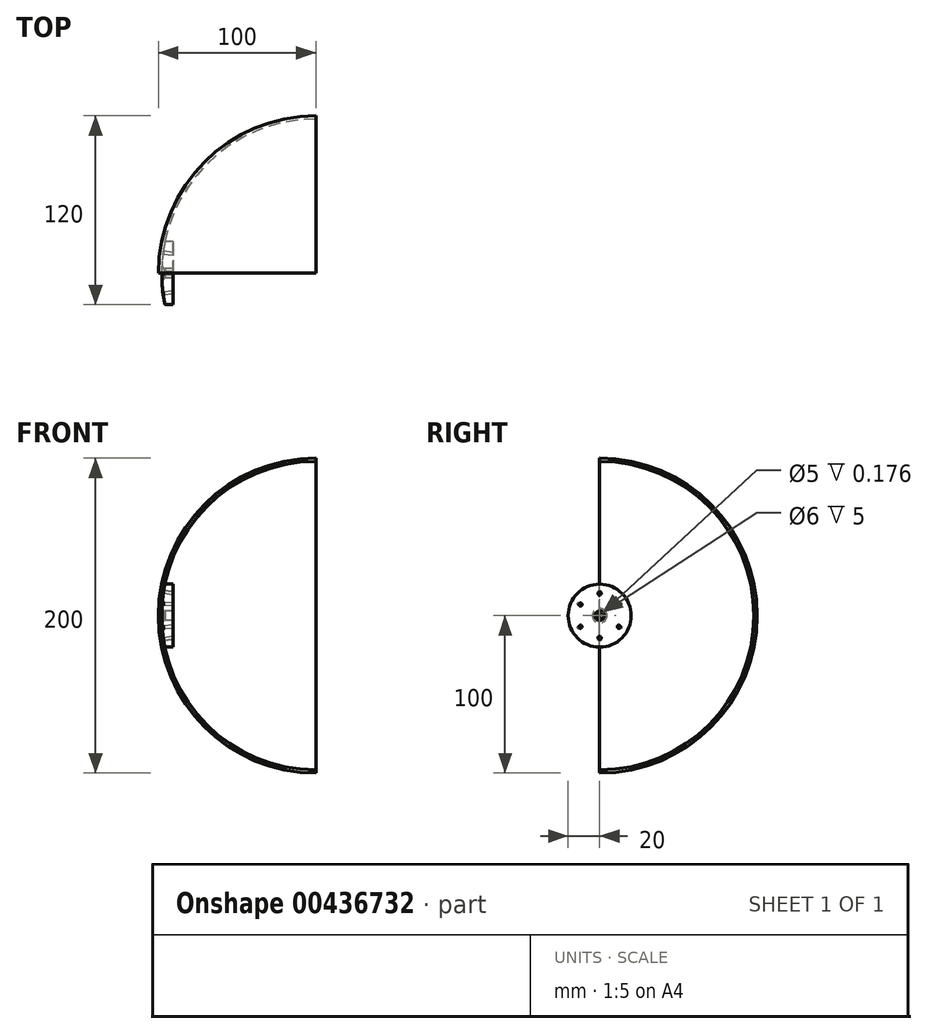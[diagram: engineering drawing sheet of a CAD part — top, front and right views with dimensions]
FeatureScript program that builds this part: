
annotation { "Feature Type Name" : "Feature", "Feature Type Description" : "" }
export const myFeature = defineFeature(function(context is Context, id is Id, definition is map)
    precondition{}
    {
        {
            var Q0;
            Q0=qCreatedBy(makeId("Front.planeOp"),FACE);
            var sketch = newSketch(context, id + "F0", { "sketchPlane" : qUnion([Q0])});
            skLineSegment(sketch, "E0", {"start": v(-108.07, 0) * mm, "end": v(24.36, 0) * mm, "construction": true});
            skLineSegment(sketch, "E1", {"start": v(0, 100) * mm, "end": v(0, 98) * mm});
            skPoint(sketch, "E2.orphan", {"position": v(0, -98) * mm});
            skPoint(sketch, "E3.orphan", {"position": v(0, -100) * mm});
            skArc(sketch, "E4", {"start": v(0, 100) * mm, "mid": v(-70.71, 70.71) * mm, "end": v(-100, 0) * mm});
            skArc(sketch, "E5", {"start": v(0, 98) * mm, "mid": v(-69.3, 69.3) * mm, "end": v(-98, 0) * mm});
            skLineSegment(sketch, "E6", {"start": v(-100, 0) * mm, "end": v(-98, 0) * mm});
            skSolve(sketch);
        }
        {
            var Q0;
            Q0 = qSketchRegion(id + "F0", true);
            var Q1;
            Q1=sQuery(id+"F0.wireOp",EDGE,"E0");
            revolve(context, id + "F1", {"entities" : qUnion([Q0]), "axis" : qUnion([Q1]), "revolveType" : RevolveType.ONE_DIRECTION, "oppositeDirection" : true, "angle" : 180 * degree});
        }
        {
            var Q0;
            Q0=qCreatedBy(makeId("Front.planeOp"),FACE);
            var sketch = newSketch(context, id + "F2", { "sketchPlane" : qUnion([Q0])});
            skArc(sketch, "E7", {"start": v(-95.94, 20) * mm, "mid": v(-97.35, 11.3) * mm, "end": v(-97.97, 2.5) * mm});
            skLineSegment(sketch, "E8", {"start": v(-90.72, 20) * mm, "end": v(-90.72, 3) * mm});
            skLineSegment(sketch, "E9", {"start": v(-95.94, 20) * mm, "end": v(-90.72, 20) * mm});
            skLineSegment(sketch, "E10", {"start": v(-90.72, 3) * mm, "end": v(-95.72, 3) * mm});
            skLineSegment(sketch, "E11", {"start": v(-95.72, 3) * mm, "end": v(-95.72, 2.5) * mm});
            skLineSegment(sketch, "E12", {"start": v(-95.72, 2.5) * mm, "end": v(-97.97, 2.5) * mm});
            skSolve(sketch);
        }
        {
            var Q0;
            Q0 = qSketchRegion(id + "F2", true);
            var Q1;
            Q1=sQuery(id+"F0.wireOp",EDGE,"E0");
            revolve(context, id + "F3", {"entities" : qUnion([Q0]), "axis" : qUnion([Q1]), "revolveType" : RevolveType.FULL});
        }
        {
            var Q0;
            Q0=qCreatedBy(makeId("Front.planeOp"),FACE);
            var sketch = newSketch(context, id + "F4", { "sketchPlane" : qUnion([Q0])});
            skLineSegment(sketch, "E13", {"start": v(-108.32, 16.78) * mm, "end": v(-86.69, 13.43) * mm, "construction": true});
            skPoint(sketch, "E14", {"position": v(-96.85, 15) * mm});
            skLineSegment(sketch, "E15", {"start": v(-97, 14.01) * mm, "end": v(-90.72, 13.04) * mm});
            skLineSegment(sketch, "E16", {"start": v(-90.57, 14.03) * mm, "end": v(-90.72, 13.04) * mm});
            skLineSegment(sketch, "E17", {"start": v(-90.57, 14.03) * mm, "end": v(-96.85, 15) * mm});
            skArc(sketch, "E18", {"start": v(-97, 14.01) * mm, "mid": v(-96.92, 14.5) * mm, "end": v(-96.85, 15) * mm});
            skSolve(sketch);
        }
        {
            var Q0;
            Q0 = qSketchRegion(id + "F4", true);
            var Q1;
            Q1=sQuery(id+"F4.wireOp",EDGE,"E13");
            revolve(context, id + "F5", {"entities" : qUnion([Q0]), "axis" : qUnion([Q1]), "revolveType" : RevolveType.FULL});
        }
        {
            var Q0;
            Q0=makeQuery(id+"F5.opRevolve","SWEPT_BODY",BODY,{"disambiguationData":[OSD([sQuery(id+"F4.wireOp",EDGE,"E15"),sQuery(id+"F4.wireOp",EDGE,"E16"),sQuery(id+"F4.wireOp",EDGE,"E17"),sQuery(id+"F4.wireOp",EDGE,"E18")])]});
            var Q1;
            Q1=sQuery(id+"F0.wireOp",EDGE,"E0");
            circularPattern(context, id + "F6", {"entities" : qUnion([Q0]), "axis" : qUnion([Q1]), "angle" : 360 * degree, "instanceCount" : 6, "equalSpace" : true});
        }
        {
            var Q0;
            Q0=makeQuery(id+"F5.opRevolve","SWEPT_BODY",BODY,{"disambiguationData":[OSD([sQuery(id+"F4.wireOp",EDGE,"E15"),sQuery(id+"F4.wireOp",EDGE,"E16"),sQuery(id+"F4.wireOp",EDGE,"E17"),sQuery(id+"F4.wireOp",EDGE,"E18")])]});
            var Q1;
            Q1=makeQuery(id+"F6.opPattern","COPY",BODY,{"derivedFrom":makeQuery(id+"F5.opRevolve","SWEPT_BODY",BODY,{"disambiguationData":[OSD([sQuery(id+"F4.wireOp",EDGE,"E15"),sQuery(id+"F4.wireOp",EDGE,"E16"),sQuery(id+"F4.wireOp",EDGE,"E17"),sQuery(id+"F4.wireOp",EDGE,"E18")])]}),"instanceName":"2"});
            var Q2;
            Q2=makeQuery(id+"F6.opPattern","COPY",BODY,{"derivedFrom":makeQuery(id+"F5.opRevolve","SWEPT_BODY",BODY,{"disambiguationData":[OSD([sQuery(id+"F4.wireOp",EDGE,"E15"),sQuery(id+"F4.wireOp",EDGE,"E16"),sQuery(id+"F4.wireOp",EDGE,"E17"),sQuery(id+"F4.wireOp",EDGE,"E18")])]}),"instanceName":"1"});
            var Q3;
            Q3=makeQuery(id+"F6.opPattern","COPY",BODY,{"derivedFrom":makeQuery(id+"F5.opRevolve","SWEPT_BODY",BODY,{"disambiguationData":[OSD([sQuery(id+"F4.wireOp",EDGE,"E15"),sQuery(id+"F4.wireOp",EDGE,"E16"),sQuery(id+"F4.wireOp",EDGE,"E17"),sQuery(id+"F4.wireOp",EDGE,"E18")])]}),"instanceName":"3"});
            var Q4;
            Q4=makeQuery(id+"F6.opPattern","COPY",BODY,{"derivedFrom":makeQuery(id+"F5.opRevolve","SWEPT_BODY",BODY,{"disambiguationData":[OSD([sQuery(id+"F4.wireOp",EDGE,"E15"),sQuery(id+"F4.wireOp",EDGE,"E16"),sQuery(id+"F4.wireOp",EDGE,"E17"),sQuery(id+"F4.wireOp",EDGE,"E18")])]}),"instanceName":"5"});
            var Q5;
            Q5=makeQuery(id+"F6.opPattern","COPY",BODY,{"derivedFrom":makeQuery(id+"F5.opRevolve","SWEPT_BODY",BODY,{"disambiguationData":[OSD([sQuery(id+"F4.wireOp",EDGE,"E15"),sQuery(id+"F4.wireOp",EDGE,"E16"),sQuery(id+"F4.wireOp",EDGE,"E17"),sQuery(id+"F4.wireOp",EDGE,"E18")])]}),"instanceName":"4"});
            var Q6;
            Q6=makeQuery(id+"F3.opRevolve","SWEPT_BODY",BODY,{"disambiguationData":[OSD([sQuery(id+"F2.wireOp",EDGE,"E7"),sQuery(id+"F2.wireOp",EDGE,"E8"),sQuery(id+"F2.wireOp",EDGE,"E9"),sQuery(id+"F2.wireOp",EDGE,"E10"),sQuery(id+"F2.wireOp",EDGE,"E11"),sQuery(id+"F2.wireOp",EDGE,"E12")])]});
            booleanBodies(context, id + "F7", {"operationType" : BooleanOperationType.SUBTRACTION, "tools" : qUnion([Q0, Q1, Q2, Q3, Q4, Q5]), "targets" : qUnion([Q6])});
        }
        {
            var Q0;
            Q0=makeQuery(id+"F3.opRevolve","SWEPT_EDGE",EDGE,{"disambiguationData":[OSD([sQuery(id+"F2.wireOp",EDGE,"E7"),sQuery(id+"F2.wireOp",EDGE,"E12")])]});
            chamfer(context, id + "F8", {"entities" : qUnion([Q0]), "width" : 2 * mm, "tangentPropagation" : true});
        }
        {
            var Q0;
            Q0=makeQuery(id+"F3.opRevolve","SWEPT_EDGE",EDGE,{"disambiguationData":[OSD([sQuery(id+"F2.wireOp",EDGE,"E7"),sQuery(id+"F2.wireOp",EDGE,"E9")])]});
            var Q1;
            Q1=makeQuery(id+"FGQLDROwnLnbr1y_2.opRevolve","SWEPT_EDGE",EDGE,{"disambiguationData":[OSD([sQuery(id+"F1g3hkHwV6IEK7N_2.wireOp",EDGE,"oPAszlLh-aMPM-wLsk-6J6p-9Ss7DIxhGMCu"),sQuery(id+"F1g3hkHwV6IEK7N_2.wireOp",EDGE,"EC95Areo-DTkT-VyXm-M4vz-fBqFukv23tx4")])]});
            fillet(context, id + "F9", {"entities" : qUnion([Q0, Q1]), "radius" : 1 * mm, "tangentPropagation" : true, "allowEdgeOverflow" : false});
        }
    });
